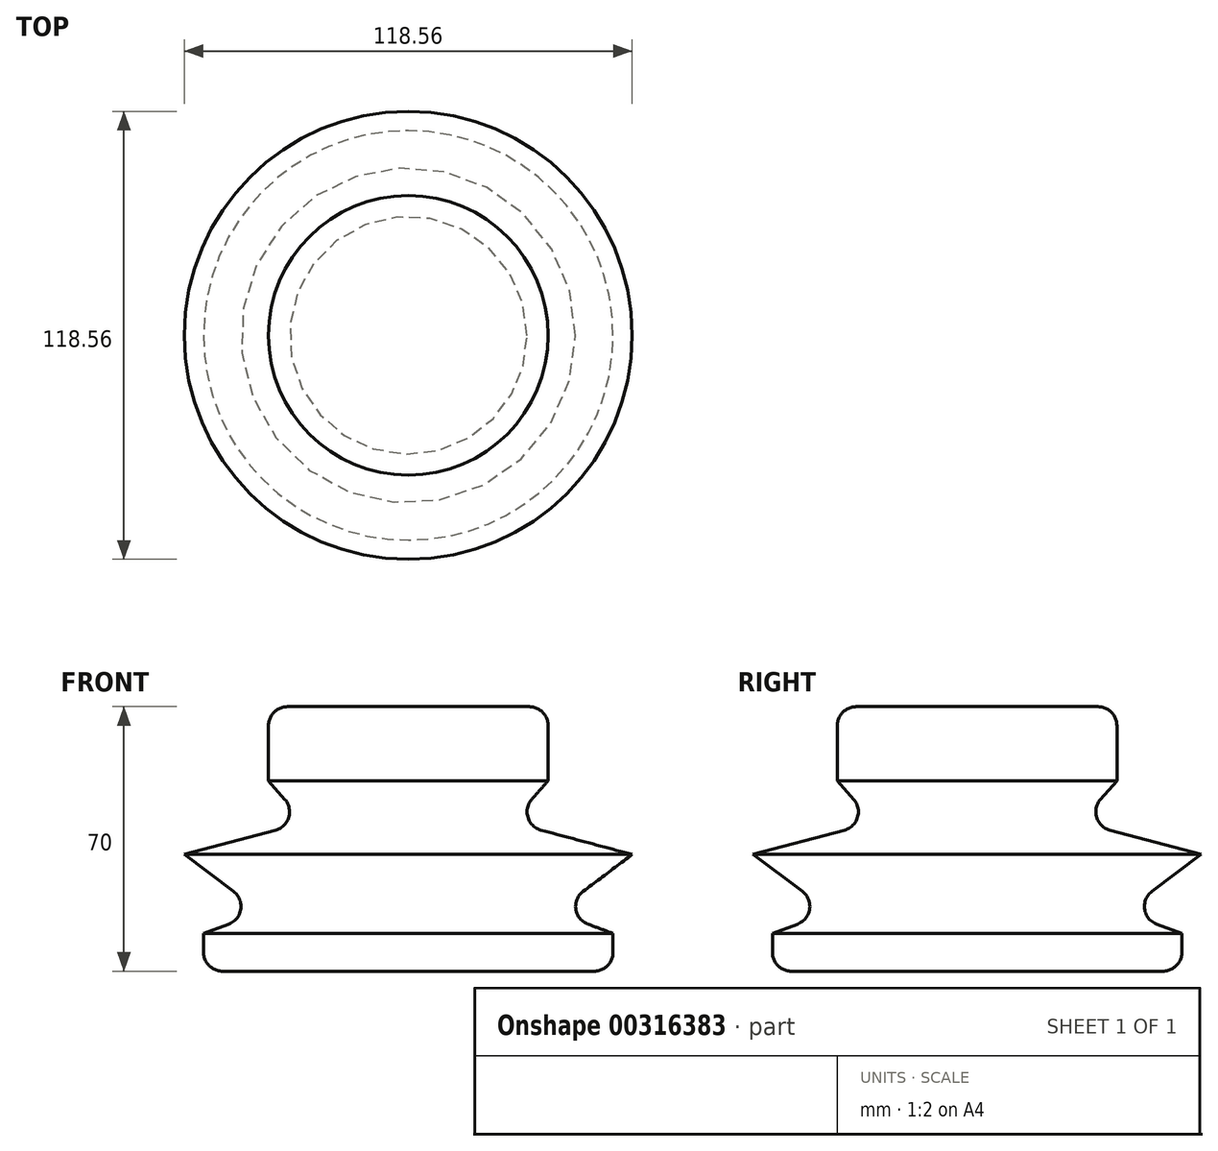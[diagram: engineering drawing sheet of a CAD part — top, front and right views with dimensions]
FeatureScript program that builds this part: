
annotation { "Feature Type Name" : "Feature", "Feature Type Description" : "" }
export const myFeature = defineFeature(function(context is Context, id is Id, definition is map)
    precondition{}
    {
        {
            var Q0;
            Q0=qCreatedBy(makeId("Front.planeOp"),FACE);
            var sketch = newSketch(context, id + "F0", { "sketchPlane" : qUnion([Q0])});
            skLineSegment(sketch, "E0", {"start": v(0, 0) * mm, "end": v(0, 65) * mm});
            skLineSegment(sketch, "E1", {"start": v(5, 70) * mm, "end": v(32, 70) * mm});
            skLineSegment(sketch, "E2", {"start": v(37, 65) * mm, "end": v(37, 50.42) * mm});
            skLineSegment(sketch, "E3", {"start": v(37, 50.42) * mm, "end": v(32.67, 45.45) * mm});
            skLineSegment(sketch, "E4", {"start": v(35.15, 37.33) * mm, "end": v(59.28, 30.88) * mm});
            skLineSegment(sketch, "E5", {"start": v(59.28, 30.88) * mm, "end": v(46.28, 21.13) * mm});
            skLineSegment(sketch, "E6", {"start": v(47.54, 12.44) * mm, "end": v(54.2, 9.98) * mm});
            skLineSegment(sketch, "E7", {"start": v(54.2, 9.98) * mm, "end": v(54.2, 5) * mm});
            skLineSegment(sketch, "E8", {"start": v(49.2, 0) * mm, "end": v(0, 0) * mm});
            skLineSegment(sketch, "E9", {"start": v(0, 75.3) * mm, "end": v(0, -42.6) * mm, "construction": true});
            skPoint(sketch, "E10.visualSharp", {"position": v(37, 70) * mm});
            skArc(sketch, "E10.filletArc", {"start": v(37, 65) * mm, "mid": v(35.54, 68.54) * mm, "end": v(32, 70) * mm});
            skPoint(sketch, "E11.visualSharp", {"position": v(0, 70) * mm});
            skArc(sketch, "E11.filletArc", {"start": v(5, 70) * mm, "mid": v(1.46, 68.54) * mm, "end": v(0, 65) * mm});
            skPoint(sketch, "E12.visualSharp", {"position": v(27.4, 39.4) * mm});
            skArc(sketch, "E12.filletArc", {"start": v(32.67, 45.45) * mm, "mid": v(31.65, 40.7) * mm, "end": v(35.15, 37.33) * mm});
            skPoint(sketch, "E13.visualSharp", {"position": v(38.94, 15.63) * mm});
            skArc(sketch, "E13.filletArc", {"start": v(46.28, 21.13) * mm, "mid": v(44.33, 16.41) * mm, "end": v(47.54, 12.44) * mm});
            skPoint(sketch, "E14.visualSharp", {"position": v(54.2, 0) * mm});
            skArc(sketch, "E14.filletArc", {"start": v(49.2, 0) * mm, "mid": v(52.73, 1.46) * mm, "end": v(54.2, 5) * mm});
            skSolve(sketch);
        }
        {
            var Q0;
            Q0=makeQuery(id+"F0.imprint","IMPRINT",FACE,{"disambiguationData":[TD([[makeQuery(id+"F0.imprint","IMPRINT",EDGE,{"derivedFrom":sQuery(id+"F0.wireOp",EDGE,"E0")}),-1.0]])]});
            var Q1;
            Q1=sQuery(id+"F0.wireOp",EDGE,"E9");
            revolve(context, id + "F1", {"entities" : qUnion([Q0]), "axis" : qUnion([Q1]), "revolveType" : RevolveType.FULL});
        }
    });
